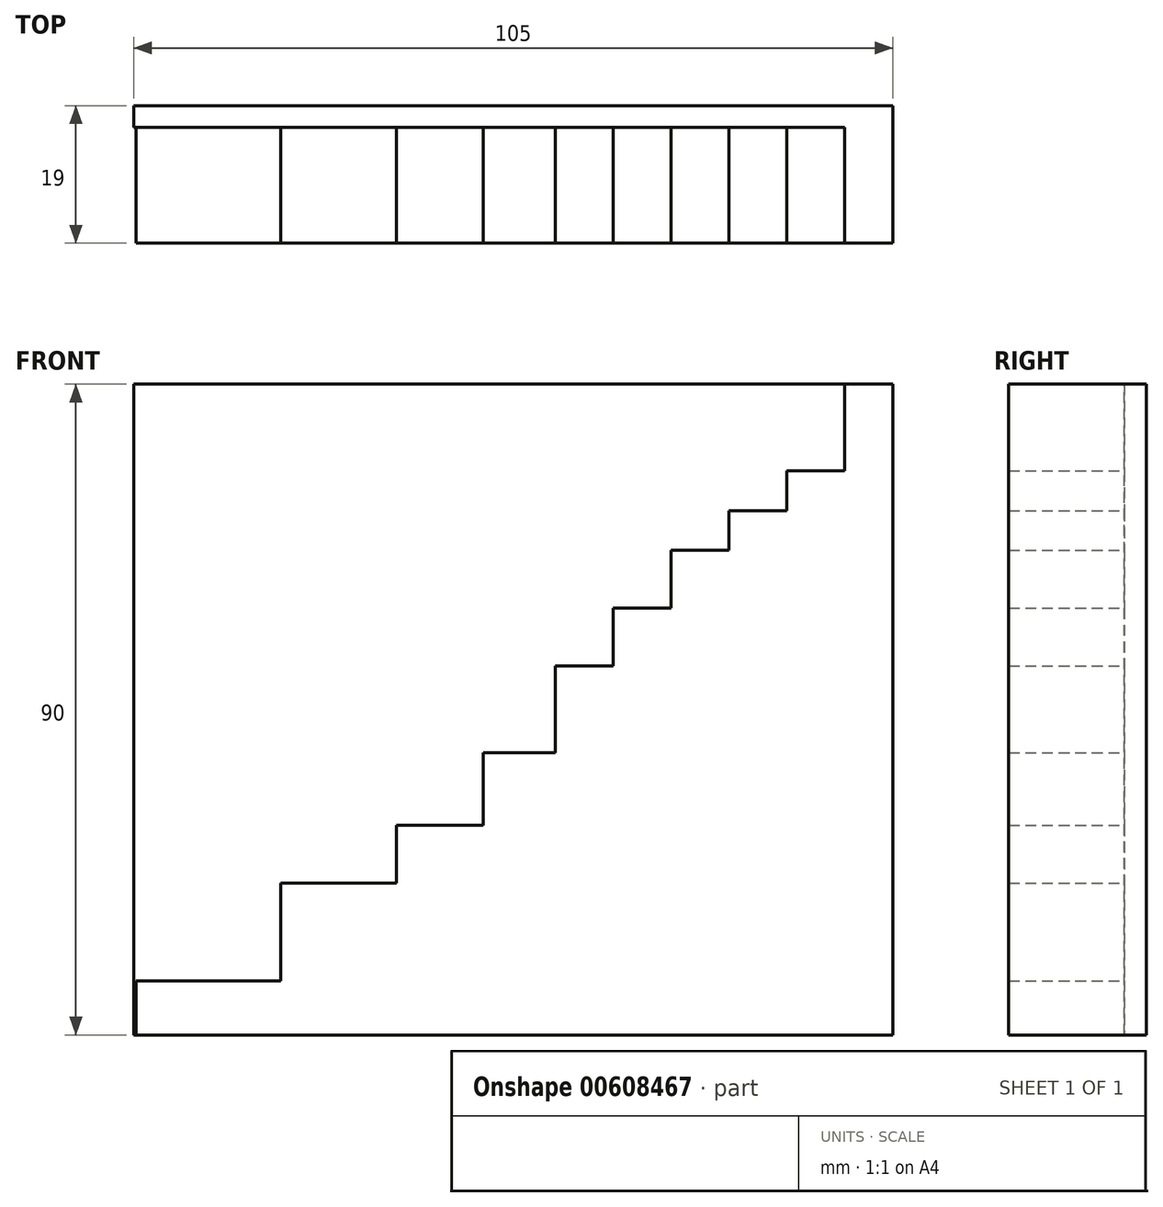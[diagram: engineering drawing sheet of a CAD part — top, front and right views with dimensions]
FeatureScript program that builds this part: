
annotation { "Feature Type Name" : "Feature", "Feature Type Description" : "" }
export const myFeature = defineFeature(function(context is Context, id is Id, definition is map)
    precondition{}
    {
        {
            var Q0;
            Q0=qCreatedBy(makeId("Front.planeOp"),FACE);
            var sketch = newSketch(context, id + "F0", { "sketchPlane" : qUnion([Q0])});
            skLineSegment(sketch, "E0.bottom", {"start": v(0, 0) * mm, "end": v(-105, 0) * mm});
            skLineSegment(sketch, "E0.top", {"start": v(0, 90) * mm, "end": v(-105, 90) * mm});
            skLineSegment(sketch, "E0.left", {"start": v(0, 0) * mm, "end": v(0, 90) * mm});
            skLineSegment(sketch, "E0.right", {"start": v(-105, 0) * mm, "end": v(-105, 90) * mm});
            skSolve(sketch);
        }
        {
            var Q0;
            Q0=makeQuery(id+"F0.imprint","IMPRINT",FACE,{"disambiguationData":[TD([[makeQuery(id+"F0.imprint","IMPRINT",EDGE,{"derivedFrom":sQuery(id+"F0.wireOp",EDGE,"E0.bottom")}),-1.0]])]});
            extrude(context, id + "F1", {"entities" : qUnion([Q0]), "depth" : 3 * mm, "offsetDistance" : 25 * mm});
        }
        {
            var Q0;
            Q0=makeQuery(id+"F1.opExtrude","CAP_FACE",FACE,{"disambiguationData":[OSD([sQuery(id+"F0.wireOp",EDGE,"E0.bottom"),sQuery(id+"F0.wireOp",EDGE,"E0.top"),sQuery(id+"F0.wireOp",EDGE,"E0.left"),sQuery(id+"F0.wireOp",EDGE,"E0.right")])],"isStart":false});
            var sketch = newSketch(context, id + "F2", { "sketchPlane" : qUnion([Q0])});
            skLineSegment(sketch, "E1", {"start": v(-104.67, 83.28) * mm, "end": v(-84.67, 83.28) * mm, "construction": true});
            skLineSegment(sketch, "E2", {"start": v(-84.67, 83.28) * mm, "end": v(-68.67, 83.28) * mm, "construction": true});
            skLineSegment(sketch, "E3", {"start": v(-68.67, 83.28) * mm, "end": v(-56.67, 83.28) * mm, "construction": true});
            skLineSegment(sketch, "E4", {"start": v(-56.67, 83.28) * mm, "end": v(-46.67, 83.28) * mm, "construction": true});
            skLineSegment(sketch, "E5", {"start": v(-46.67, 83.28) * mm, "end": v(-38.67, 83.28) * mm, "construction": true});
            skLineSegment(sketch, "E6", {"start": v(-38.67, 83.28) * mm, "end": v(-30.67, 83.28) * mm, "construction": true});
            skLineSegment(sketch, "E7", {"start": v(-30.67, 83.28) * mm, "end": v(-22.67, 83.28) * mm, "construction": true});
            skLineSegment(sketch, "E8", {"start": v(-22.67, 83.28) * mm, "end": v(-14.67, 83.28) * mm, "construction": true});
            skLineSegment(sketch, "E9", {"start": v(-14.67, 83.28) * mm, "end": v(-6.67, 83.28) * mm, "construction": true});
            skLineSegment(sketch, "E10", {"start": v(-6.67, 83.28) * mm, "end": v(0, 83.28) * mm, "construction": true});
            skLineSegment(sketch, "E11", {"start": v(0, 90) * mm, "end": v(-6.67, 90) * mm});
            skLineSegment(sketch, "E12", {"start": v(-6.67, 90) * mm, "end": v(-6.67, 78) * mm});
            skLineSegment(sketch, "E13", {"start": v(-6.67, 78) * mm, "end": v(-14.67, 78) * mm});
            skLineSegment(sketch, "E14", {"start": v(-14.67, 78) * mm, "end": v(-14.67, 72.5) * mm});
            skLineSegment(sketch, "E15", {"start": v(-14.67, 72.5) * mm, "end": v(-22.67, 72.5) * mm});
            skLineSegment(sketch, "E16", {"start": v(-22.67, 72.5) * mm, "end": v(-22.67, 67) * mm});
            skLineSegment(sketch, "E17", {"start": v(-22.67, 67) * mm, "end": v(-30.67, 67) * mm});
            skLineSegment(sketch, "E18", {"start": v(-30.67, 67) * mm, "end": v(-30.67, 59) * mm});
            skLineSegment(sketch, "E19", {"start": v(-30.67, 59) * mm, "end": v(-38.67, 59) * mm});
            skLineSegment(sketch, "E20", {"start": v(-38.67, 59) * mm, "end": v(-38.67, 51) * mm});
            skLineSegment(sketch, "E21", {"start": v(-38.67, 51) * mm, "end": v(-46.67, 51) * mm});
            skLineSegment(sketch, "E22", {"start": v(-46.67, 51) * mm, "end": v(-46.67, 39) * mm});
            skLineSegment(sketch, "E23", {"start": v(-46.67, 39) * mm, "end": v(-56.67, 39) * mm});
            skLineSegment(sketch, "E24", {"start": v(-56.67, 39) * mm, "end": v(-56.67, 29) * mm});
            skLineSegment(sketch, "E25", {"start": v(-56.67, 29) * mm, "end": v(-68.67, 29) * mm});
            skLineSegment(sketch, "E26", {"start": v(-68.67, 29) * mm, "end": v(-68.67, 21) * mm});
            skLineSegment(sketch, "E27", {"start": v(-68.67, 21) * mm, "end": v(-84.67, 21) * mm});
            skLineSegment(sketch, "E28", {"start": v(-84.67, 21) * mm, "end": v(-84.67, 7.5) * mm});
            skLineSegment(sketch, "E29", {"start": v(-84.67, 7.5) * mm, "end": v(-104.67, 7.5) * mm});
            skLineSegment(sketch, "E30", {"start": v(-104.67, 7.5) * mm, "end": v(-104.67, 0) * mm});
            skLineSegment(sketch, "E31", {"start": v(-104.67, 0) * mm, "end": v(0, 0) * mm});
            skLineSegment(sketch, "E32", {"start": v(0, 0) * mm, "end": v(0, 90) * mm});
            skSolve(sketch);
        }
        {
            var Q0;
            Q0=makeQuery(id+"F2.imprint","IMPRINT",FACE,{"disambiguationData":[TD([[makeQuery(id+"F2.imprint","IMPRINT",EDGE,{"derivedFrom":sQuery(id+"F2.wireOp",EDGE,"E11")}),1.0]])]});
            extrude(context, id + "F3", {"entities" : qUnion([Q0]), "operationType" : NewBodyOperationType.ADD, "depth" : 16 * mm, "offsetDistance" : 25 * mm});
        }
    });
